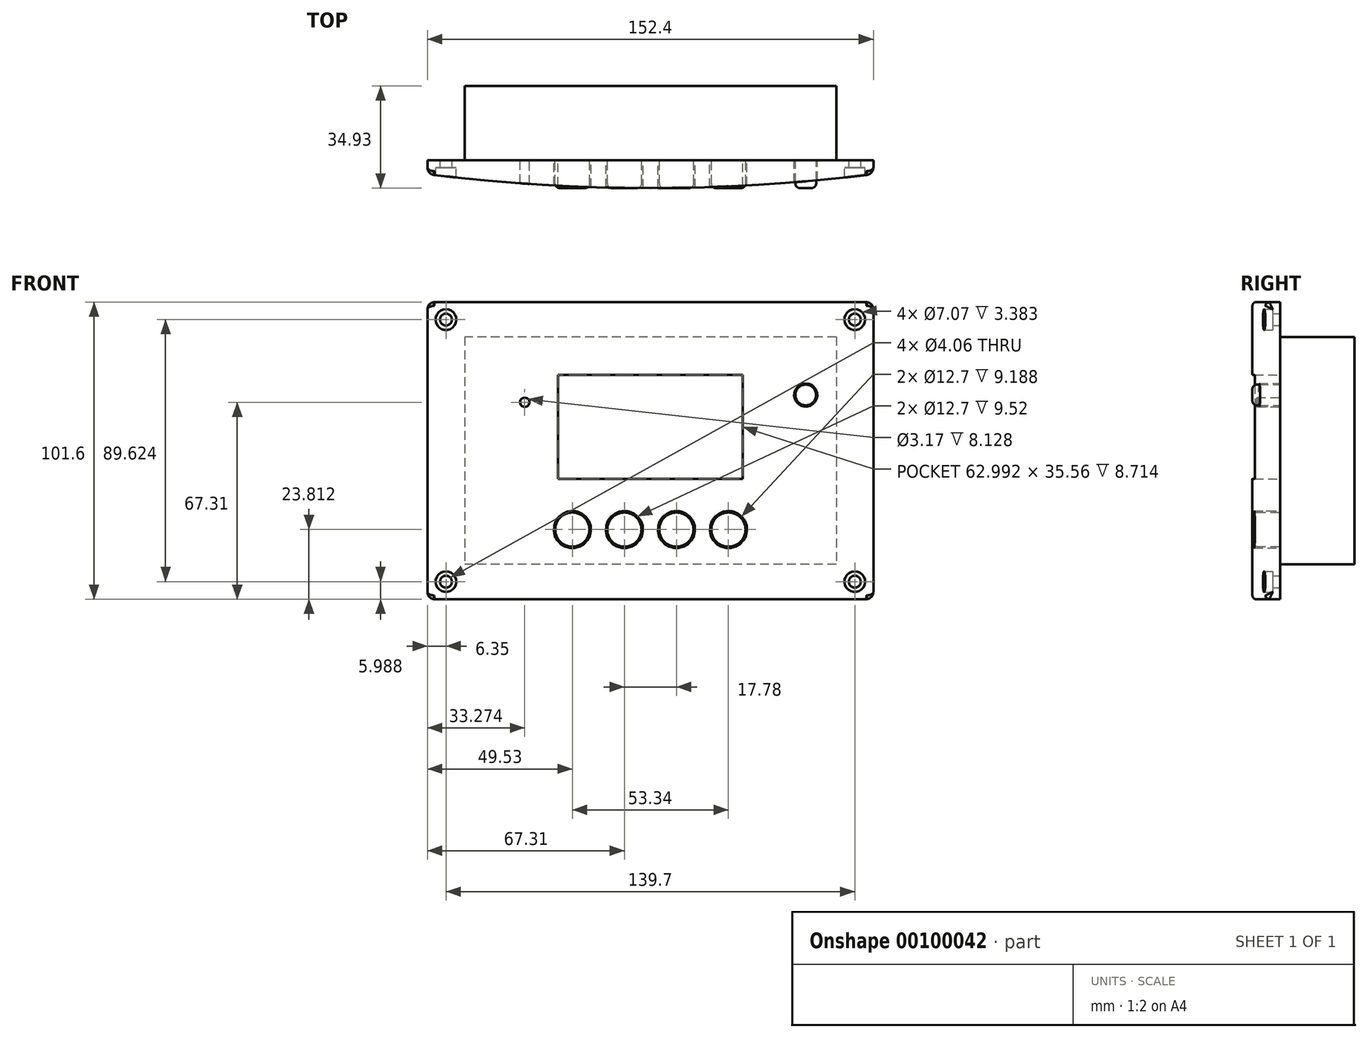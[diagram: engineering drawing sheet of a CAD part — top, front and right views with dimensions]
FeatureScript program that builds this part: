
annotation { "Feature Type Name" : "Feature", "Feature Type Description" : "" }
export const myFeature = defineFeature(function(context is Context, id is Id, definition is map)
    precondition{}
    {
        {
            var Q0;
            Q0=qCreatedBy(makeId("Front.planeOp"),FACE);
            var sketch = newSketch(context, id + "F0", { "sketchPlane" : qUnion([Q0])});
            skLineSegment(sketch, "E0.bottom", {"start": v(63.5, 38.9) * mm, "end": v(-63.5, 38.9) * mm});
            skLineSegment(sketch, "E0.top", {"start": v(63.5, -38.9) * mm, "end": v(-63.5, -38.9) * mm});
            skLineSegment(sketch, "E0.left", {"start": v(63.5, 38.9) * mm, "end": v(63.5, -38.9) * mm});
            skLineSegment(sketch, "E0.right", {"start": v(-63.5, 38.9) * mm, "end": v(-63.5, -38.9) * mm});
            skPoint(sketch, "E0.middle", {"position": v(0, 0) * mm});
            skSolve(sketch);
        }
        {
            var Q0;
            Q0=makeQuery(id+"F0.imprint","IMPRINT",FACE,{"disambiguationData":[TD([[makeQuery(id+"F0.imprint","IMPRINT",EDGE,{"derivedFrom":sQuery(id+"F0.wireOp",EDGE,"E0.bottom")}),1.0]])]});
            extrude(context, id + "F1", {"entities" : qUnion([Q0]), "oppositeDirection" : true, "depth" : 25.4 * mm});
        }
        {
            var Q0;
            Q0=qCreatedBy(makeId("Top.planeOp"),FACE);
            var sketch = newSketch(context, id + "F2", { "sketchPlane" : qUnion([Q0])});
            skLineSegment(sketch, "E1", {"start": v(-76.2, 0) * mm, "end": v(76.2, 0) * mm});
            skLineSegment(sketch, "E2", {"start": v(0, 0) * mm, "end": v(0, -9.52) * mm, "construction": true});
            skLineSegment(sketch, "E3", {"start": v(-76.2, 0) * mm, "end": v(-76.2, -4.76) * mm});
            skLineSegment(sketch, "E4", {"start": v(76.2, 0) * mm, "end": v(76.2, -4.76) * mm});
            skArc(sketch, "E5", {"start": v(-76.2, -4.76) * mm, "mid": v(0, -9.53) * mm, "end": v(76.2, -4.76) * mm});
            skSolve(sketch);
        }
        {
            var Q0;
            Q0 = qSketchRegion(id + "F2", true);
            extrude(context, id + "F3", {"entities" : qUnion([Q0]), "operationType" : NewBodyOperationType.ADD, "depth" : 101.6 * mm, "symmetric" : true});
        }
        {
            var Q0;
            Q0=makeQuery(id+"F3.opExtrude","SWEPT_FACE",FACE,{"disambiguationData":[OSD([sQuery(id+"F2.wireOp",EDGE,"E1")])]});
            var sketch = newSketch(context, id + "F4", { "sketchPlane" : qUnion([Q0])});
            skLineSegment(sketch, "E6.bottom", {"start": v(-69.85, 44.81) * mm, "end": v(69.85, 44.81) * mm, "construction": true});
            skLineSegment(sketch, "E6.top", {"start": v(-69.85, -44.81) * mm, "end": v(69.85, -44.81) * mm, "construction": true});
            skLineSegment(sketch, "E6.left", {"start": v(-69.85, 44.81) * mm, "end": v(-69.85, -44.81) * mm, "construction": true});
            skLineSegment(sketch, "E6.right", {"start": v(69.85, 44.81) * mm, "end": v(69.85, -44.81) * mm, "construction": true});
            skLineSegment(sketch, "E7", {"start": v(-69.85, 44.81) * mm, "end": v(-63.5, 38.9) * mm, "construction": true});
            skLineSegment(sketch, "E8", {"start": v(63.5, 38.9) * mm, "end": v(69.85, 44.81) * mm, "construction": true});
            skLineSegment(sketch, "E9", {"start": v(63.5, -38.9) * mm, "end": v(69.85, -44.81) * mm, "construction": true});
            skLineSegment(sketch, "E10", {"start": v(-63.5, -38.9) * mm, "end": v(-69.85, -44.81) * mm, "construction": true});
            skCircle(sketch, "E11", {"center": v(-69.85, 44.81) * mm, "radius": 3.54 * mm});
            skCircle(sketch, "E12", {"center": v(-69.85, -44.81) * mm, "radius": 3.54 * mm});
            skCircle(sketch, "E13", {"center": v(69.85, -44.81) * mm, "radius": 3.54 * mm});
            skCircle(sketch, "E14", {"center": v(69.85, 44.81) * mm, "radius": 3.54 * mm});
            skSolve(sketch);
        }
        {
            var Q0;
            Q0 = qSketchRegion(id + "F4", true);
            extrude(context, id + "F5", {"entities" : qUnion([Q0]), "operationType" : NewBodyOperationType.REMOVE, "oppositeDirection" : true, "depth" : 25.4 * mm});
        }
        {
            var Q0;
            Q0=makeQuery(id+"F3.opExtrude","SWEPT_FACE",FACE,{"disambiguationData":[OSD([sQuery(id+"F2.wireOp",EDGE,"E1")])]});
            var sketch = newSketch(context, id + "F6", { "sketchPlane" : qUnion([Q0])});
            skCircle(sketch, "E15.0", {"center": v(-69.85, 44.81) * mm, "radius": 3.54 * mm});
            skCircle(sketch, "E15.1", {"center": v(-69.85, -44.81) * mm, "radius": 3.54 * mm});
            skCircle(sketch, "E15.2", {"center": v(69.85, -44.81) * mm, "radius": 3.54 * mm});
            skCircle(sketch, "E15.3", {"center": v(69.85, 44.81) * mm, "radius": 3.54 * mm});
            skCircle(sketch, "E16", {"center": v(-69.85, 44.81) * mm, "radius": 2.03 * mm});
            skCircle(sketch, "E17", {"center": v(69.85, 44.81) * mm, "radius": 2.03 * mm});
            skCircle(sketch, "E18", {"center": v(69.85, -44.81) * mm, "radius": 2.03 * mm});
            skCircle(sketch, "E19", {"center": v(-69.85, -44.81) * mm, "radius": 2.03 * mm});
            skSolve(sketch);
        }
        {
            var Q0;
            Q0 = qSketchRegion(id + "F6", true);
            extrude(context, id + "F7", {"entities" : qUnion([Q0]), "operationType" : NewBodyOperationType.ADD, "oppositeDirection" : true, "depth" : 2.54 * mm});
        }
        {
            var Q0;
            Q0=qCreatedBy(makeId("Front.planeOp"),FACE);
            var sketch = newSketch(context, id + "F8", { "sketchPlane" : qUnion([Q0])});
            skLineSegment(sketch, "E20.bottom", {"start": v(-31.5, 25.9) * mm, "end": v(31.5, 25.9) * mm});
            skLineSegment(sketch, "E20.top", {"start": v(-31.5, -9.65) * mm, "end": v(31.5, -9.65) * mm});
            skLineSegment(sketch, "E20.left", {"start": v(-31.5, 25.9) * mm, "end": v(-31.5, -9.65) * mm});
            skLineSegment(sketch, "E20.right", {"start": v(31.5, 25.9) * mm, "end": v(31.5, -9.65) * mm});
            skLineSegment(sketch, "E21", {"start": v(0, 0) * mm, "end": v(31.5, 0) * mm, "construction": true});
            skLineSegment(sketch, "E22", {"start": v(0, 0) * mm, "end": v(-31.5, 0) * mm, "construction": true});
            skCircle(sketch, "E23", {"center": v(53.09, 19.05) * mm, "radius": 3.97 * mm});
            skCircle(sketch, "E24", {"center": v(-42.93, 16.5) * mm, "radius": 1.59 * mm});
            skCircle(sketch, "E25", {"center": v(-26.67, -26.99) * mm, "radius": 6.35 * mm});
            skCircle(sketch, "E26", {"center": v(-8.9, -26.99) * mm, "radius": 6.35 * mm});
            skCircle(sketch, "E27", {"center": v(8.9, -26.99) * mm, "radius": 6.35 * mm});
            skCircle(sketch, "E28", {"center": v(26.67, -26.99) * mm, "radius": 6.35 * mm});
            skLineSegment(sketch, "E29", {"start": v(-26.67, -26.99) * mm, "end": v(-8.9, -26.99) * mm, "construction": true});
            skLineSegment(sketch, "E30", {"start": v(-8.9, -26.99) * mm, "end": v(8.9, -26.99) * mm, "construction": true});
            skLineSegment(sketch, "E31", {"start": v(8.9, -26.99) * mm, "end": v(26.67, -26.99) * mm, "construction": true});
            skLineSegment(sketch, "E32", {"start": v(0, -26.99) * mm, "end": v(0, 0) * mm, "construction": true});
            skSolve(sketch);
        }
        {
            var Q0;
            Q0 = qSketchRegion(id + "F8", true);
            extrude(context, id + "F9", {"entities" : qUnion([Q0]), "operationType" : NewBodyOperationType.REMOVE, "depth" : 25.4 * mm});
        }
        {
            var Q0;
            Q0=makeQuery(id+"F9.boolean.opBoolean","COPY",FACE,{"derivedFrom":makeQuery(id+"F9.opExtrude","CAP_FACE",FACE,{"disambiguationData":[OSD([sQuery(id+"F8.wireOp",EDGE,"E27")])],"isStart":true})});
            var sketch = newSketch(context, id + "F10", { "sketchPlane" : qUnion([Q0])});
            skCircle(sketch, "E33", {"center": v(-26.67, -26.99) * mm, "radius": 5.84 * mm});
            skCircle(sketch, "E34", {"center": v(-8.9, -26.99) * mm, "radius": 5.84 * mm});
            skCircle(sketch, "E35", {"center": v(8.9, -26.99) * mm, "radius": 5.84 * mm});
            skCircle(sketch, "E36", {"center": v(26.67, -26.99) * mm, "radius": 5.84 * mm});
            skCircle(sketch, "E37", {"center": v(53.09, 19.05) * mm, "radius": 3.56 * mm});
            skSolve(sketch);
        }
        {
            var Q0;
            Q0 = qSketchRegion(id + "F10", true);
            extrude(context, id + "F11", {"entities" : qUnion([Q0]), "operationType" : NewBodyOperationType.ADD, "depth" : 9.52 * mm});
        }
        {
            var Q0;
            Q0=makeQuery(id+"F11.opExtrude","CAP_FACE",FACE,{"disambiguationData":[OSD([sQuery(id+"F10.wireOp",EDGE,"E36")])],"isStart":false});
            var Q1;
            Q1=makeQuery(id+"F11.opExtrude","CAP_EDGE",EDGE,{"disambiguationData":[OSD([sQuery(id+"F10.wireOp",EDGE,"E35")])],"isStart":false});
            var Q2;
            Q2=makeQuery(id+"F11.opExtrude","CAP_EDGE",EDGE,{"disambiguationData":[OSD([sQuery(id+"F10.wireOp",EDGE,"E34")])],"isStart":false});
            var Q3;
            Q3=makeQuery(id+"F11.opExtrude","CAP_EDGE",EDGE,{"disambiguationData":[OSD([sQuery(id+"F10.wireOp",EDGE,"E33")])],"isStart":false});
            var Q4;
            Q4=makeQuery(id+"F11.opExtrude","CAP_EDGE",EDGE,{"disambiguationData":[OSD([sQuery(id+"F10.wireOp",EDGE,"E37")])],"isStart":false});
            fillet(context, id + "F12", {"entities" : qUnion([Q0, Q1, Q2, Q3, Q4]), "radius" : 1.52 * mm, "allowEdgeOverflow" : false});
        }
        {
            var Q0;
            Q0=makeQuery(id+"F3.opExtrude","SWEPT_EDGE",EDGE,{"disambiguationData":[OSD([sQuery(id+"F2.wireOp",EDGE,"E3"),sQuery(id+"F2.wireOp",EDGE,"E5")])]});
            var Q1;
            Q1=makeQuery(id+"F3.opExtrude","SWEPT_EDGE",EDGE,{"disambiguationData":[OSD([sQuery(id+"F2.wireOp",EDGE,"E4"),sQuery(id+"F2.wireOp",EDGE,"E5")])]});
            var Q2;
            Q2=makeQuery(id+"F3.opExtrude","CAP_EDGE",EDGE,{"disambiguationData":[OSD([sQuery(id+"F2.wireOp",EDGE,"E4")])],"isStart":false});
            var Q3;
            Q3=makeQuery(id+"F3.opExtrude","CAP_EDGE",EDGE,{"disambiguationData":[OSD([sQuery(id+"F2.wireOp",EDGE,"E4")])],"isStart":true});
            var Q4;
            Q4=makeQuery(id+"F3.opExtrude","CAP_EDGE",EDGE,{"disambiguationData":[OSD([sQuery(id+"F2.wireOp",EDGE,"E3")])],"isStart":true});
            var Q5;
            Q5=makeQuery(id+"F3.opExtrude","CAP_EDGE",EDGE,{"disambiguationData":[OSD([sQuery(id+"F2.wireOp",EDGE,"E3")])],"isStart":false});
            fillet(context, id + "F13", {"entities" : qUnion([Q0, Q1, Q2, Q3, Q4, Q5]), "radius" : 2.54 * mm, "tangentPropagation" : true, "allowEdgeOverflow" : false});
        }
        {
            var Q0;
            Q0=makeQuery(id+"F3.opExtrude","CAP_EDGE",EDGE,{"disambiguationData":[OSD([sQuery(id+"F2.wireOp",EDGE,"E5")])],"isStart":false});
            var Q1;
            Q1=makeQuery(id+"F3.opExtrude","CAP_EDGE",EDGE,{"disambiguationData":[OSD([sQuery(id+"F2.wireOp",EDGE,"E5")])],"isStart":true});
            fillet(context, id + "F14", {"entities" : qUnion([Q0, Q1]), "radius" : 1.27 * mm, "tangentPropagation" : true, "allowEdgeOverflow" : false});
        }
    });
